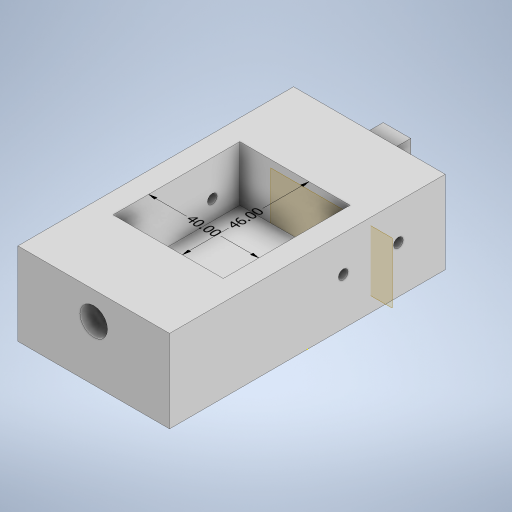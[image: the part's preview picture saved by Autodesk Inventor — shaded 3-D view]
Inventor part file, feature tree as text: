
AUTODESK INVENTOR PART (.ipt)
format: ipt  version: 2023 (Build 270158000, 158)  size: 297,472 bytes
history: native  units: mm
features: sketch x8, extrude x6, other x4, plane x3, hole x1
ambient origin geometry x8: Origin, YZ Plane, XZ Plane, XY Plane, X Axis, Y Axis, Z Axis, Center Point
bodies: Body1 (feature_tree)
feature tree (22):
  other  "Sólido1"
  other  "Anotaciones"
  extrude  "Extrusión1"  Depth=100.0mm
  extrude  "Extrusión2"  Depth=10.0mm
  extrude  "Extrusión3"  Depth=5.0mm
  extrude  "Extrusión4"  Depth=10.0mm TaperAngle=0.0deg
  plane  "Plano de trabajo1"
  extrude  "Extrusión5"  Depth=10.0mm
  plane  "Plano de trabajo2"
  extrude  "Extrusión6"  Depth=40.0mm
  sketch  "Boceto7"  dims[d15=46.0mm d16=20.0mm d17=0.0mm]
  plane  "Plano de trabajo4"
  hole  "Agujero1"  [1 undecoded]
  sketch  "Boceto1"  dims[d0=55.0mm d1=100.0mm]
  sketch  "Boceto2"  dims[d2=30.0mm d3=0.0mm d4=10.0mm]
  sketch  "Boceto3"  dims[d5=20.0mm d6=5.0mm]
  sketch  "Boceto4"  dims[d7=22.5mm d8=10.0mm d9=0.0mm]
  sketch  "Boceto5"  dims[d10=10.0mm d11=10.0mm]
  sketch  "Boceto6"  dims[d12=15.0mm d13=0.0mm d14=40.0mm]
  sketch  "Boceto8"  dims[d24=22.5mm d25=2.5mm d26=2.5mm d27=8.0mm d28=0.0mm d29=3.0mm d30=3.0mm d31=8.0mm d32=0.0mm d33=0.0mm d34=10.0mm d35=30.0mm d36=5.0mm d37=5.0mm d38=5.0mm d39=5.0mm d40=10.0mm d41=8.0mm d42=3.5mm d43=6.0mm d44=4.0mm d45=2.0mm d46=90.0deg d47=8.0mm d48=20.594885mm d18=5.462798mm d19=4.90751mm d20=46.0mm d21=4.68859mm d22=6.124374mm d23=40.0mm]
  other  "Cota lineal 1"
  other  "Cota lineal 2"
note: 1 required parameter value undecoded (feature->parameter linkage not recoverable at this tier; creation-order binding heuristic only, values carry confidence <= 0.55)
